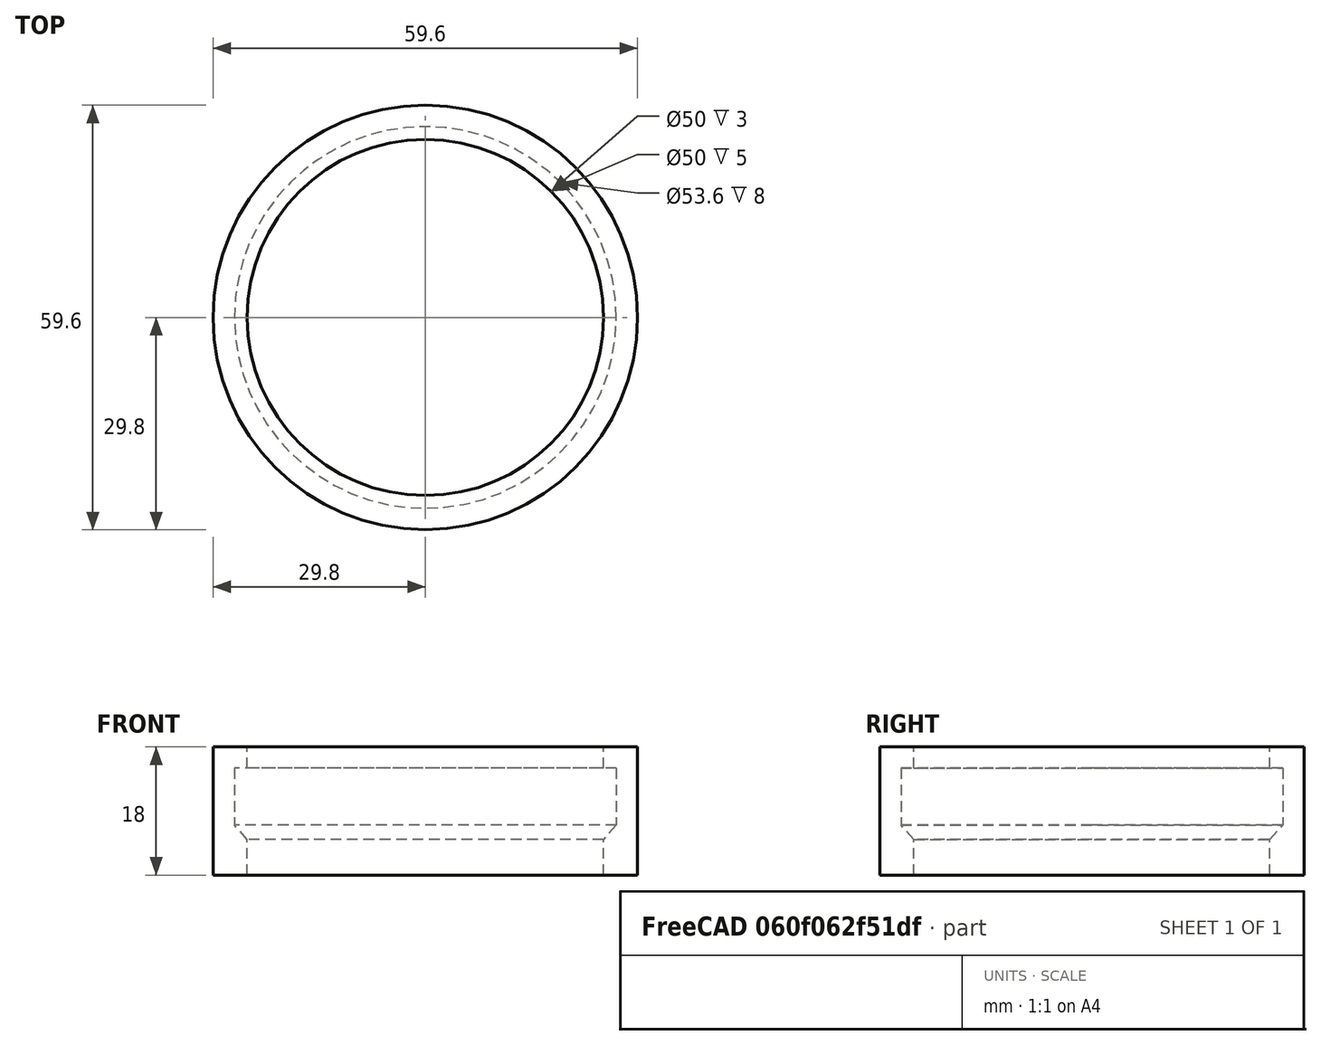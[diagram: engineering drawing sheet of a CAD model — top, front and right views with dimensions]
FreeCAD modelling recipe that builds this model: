
FCSTD DOCUMENT  (FreeCAD 1.1R39748 (Git))
Label: горло
License: All rights reserved
LicenseURL: https://en.wikipedia.org/wiki/All_rights_reserved
objects: App::Point×1, Sketcher::SketchObject×1, PartDesign::Revolution×1, PartDesign::Body×1
note: 6 computed .brp shape members not serialized (recipe doc carries the construction recipe); baked Part::Feature solids carry a one-line shape summary decoded from their .brp

FEATURE [App::Point] Origin001
  Role = Origin
FEATURE [Sketcher::SketchObject] Sketch
  ArcFitTolerance = 1e-06
  AttachmentSupport = -> [XZ_Plane]
  ExternalTypes = [0]
  FullyConstrained = true
  MakeInternals = false
  MapMode = 5
  Placement = pos=(0,0,0) rot=(1,0,0;1.5708rad)
  expr: Constraints[23] = 63 / 2 - 1.8 + 0.3
  expr: Constraints[2] = 50 / 2 + 0.5
  sketch-geometry (8):
    g0: LineSegment StartX=25.5 StartY=0 StartZ=0 EndX=25.5 EndY=5 EndZ=0
    g1: LineSegment StartX=30 StartY=17.5 StartZ=0 EndX=30 EndY=9.5 EndZ=0
    g2: LineSegment StartX=30 StartY=9.5 StartZ=0 EndX=25.5 EndY=5 EndZ=0
    g3: LineSegment StartX=30 StartY=17.5 StartZ=0 EndX=25.5 EndY=17.5 EndZ=0
    g4: LineSegment StartX=25.5 StartY=17.5 StartZ=0 EndX=25.5 EndY=20.5 EndZ=0
    g5: LineSegment StartX=25.5 StartY=20.5 StartZ=0 EndX=32 EndY=20.5 EndZ=0
    g6: LineSegment StartX=32 StartY=20.5 StartZ=0 EndX=32 EndY=0 EndZ=0
    g7: LineSegment StartX=32 StartY=0 StartZ=0 EndX=25.5 EndY=0 EndZ=0
  constraints (25):
    c: PointOnObject(g0,g-1)
    c: Vertical(g0)
    c: Distance(g0,g-1) = 25.5
    c: Vertical(g1)
    c: Coincident(g2,g0)
    c: Coincident(g1,g2)
    c: Distance(g1,g1) = 8
    c: Coincident(g3,g1)
    c: Horizontal(g3)
    c: DistanceX(g-1,g3) = 25.5
    c: Coincident(g4,g3)
    c: Vertical(g4)
    c: Coincident(g5,g4)
    c: Horizontal(g5)
    c: Coincident(g6,g5)
    c: PointOnObject(g6,g-1)
    c: Vertical(g6)
    c: Coincident(g7,g6)
    c: Coincident(g7,g0)
    c: Distance(g3,g4) = 3
    c: DistanceX(g1,g6) = 2
    c: DistanceY(g0,g0) = 5
    c: Angle(g0,g2) = 2.35619
    c: DistanceX(g-1,g1) = 30
    c: Distance(g3,g1) = 4.5
FEATURE [PartDesign::Revolution] Revolution
  Angle = 360
  Angle2 = 60
  Axis = (0,2e-16,1)
  Base = (0,0,0)
  Placement = pos=(0,0,0) rot=(1,0,0;1.5708rad)
  Profile = -> Sketch
  ReferenceAxis = -> Sketch [V_Axis]
  Reversed = true
  Suppressed = false
  Type = 0
FEATURE [PartDesign::Body] Body
  AllowCompound = false
  Group = -> [Sketch,Revolution]
  Origin = -> Origin
  Tip = -> Revolution
